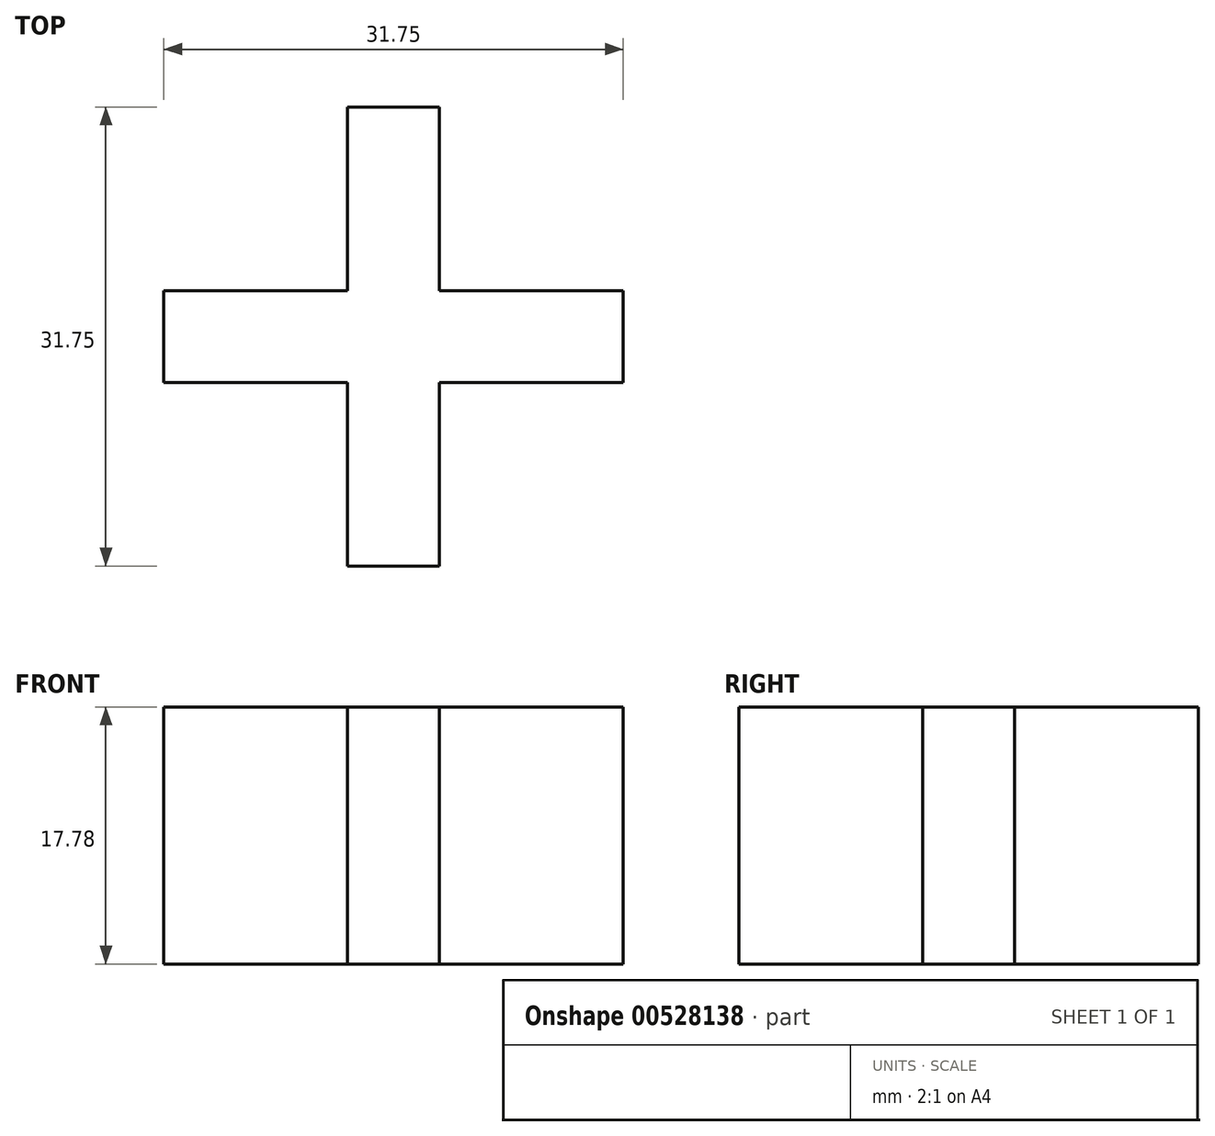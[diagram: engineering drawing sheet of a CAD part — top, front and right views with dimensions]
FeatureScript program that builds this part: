
annotation { "Feature Type Name" : "Feature", "Feature Type Description" : "" }
export const myFeature = defineFeature(function(context is Context, id is Id, definition is map)
    precondition{}
    {
        {
            var Q0;
            Q0=qCreatedBy(makeId("Top.planeOp"),FACE);
            var sketch = newSketch(context, id + "F0", { "sketchPlane" : qUnion([Q0])});
            skLineSegment(sketch, "E0.bottom", {"start": v(-22.09, 6.35) * mm, "end": v(9.66, 6.35) * mm});
            skLineSegment(sketch, "E0.top", {"start": v(-22.09, 0) * mm, "end": v(9.66, 0) * mm});
            skLineSegment(sketch, "E0.left", {"start": v(-22.09, 6.35) * mm, "end": v(-22.09, 0) * mm});
            skLineSegment(sketch, "E0.right", {"start": v(9.66, 6.35) * mm, "end": v(9.66, 0) * mm});
            skLineSegment(sketch, "E1.bottom", {"start": v(-9.39, 19.05) * mm, "end": v(-3.04, 19.05) * mm});
            skLineSegment(sketch, "E1.top", {"start": v(-9.39, -12.7) * mm, "end": v(-3.04, -12.7) * mm});
            skLineSegment(sketch, "E1.left", {"start": v(-9.39, 19.05) * mm, "end": v(-9.39, -12.7) * mm});
            skLineSegment(sketch, "E1.right", {"start": v(-3.04, 19.05) * mm, "end": v(-3.04, -12.7) * mm});
            skLineSegment(sketch, "E2.left", {"start": v(-3.04, 19.05) * mm, "end": v(-3.04, 6.35) * mm});
            skSolve(sketch);
        }
        {
            var Q0;
            Q0=qSketchRegion(id+"F0",true);
            extrude(context, id + "F1", {"entities" : qUnion([Q0]), "depth" : 17.78 * mm});
        }
    });
